# Revit family: R-MBS-225
name_source: partatom
category: Portes
units: mm (PartAtom-declared; Revit-internal decimal feet)

## family parameters
Couper avec des vides une fois chargée = Non
Hôte = Mur
Numéro OmniClass = 23.30.10.00
Partagée = Non
Repère de localisation dans la pièce = Non
Titre OmniClass = Doors
Toujours verticalement = Oui

## types (2) — shared parameters
Coloris parclose oculus = Acier, finition peinture thermolaque, gris, brillant
Construction analytique = <Aucun>
Définir les propriétés thermiques par = Type schématique
Epaisseur mur support = 146 mm
Epaisseur vantail = 40 mm  [stored 0.131234 ft]
Fermeture du mur = Par hôte
Fonction = Intérieur
Hauteur = 2000 mm  [stored 6.56168 ft]
Hauteur axe poignée = 1045 mm  [stored 3.42848 ft]
Hauteur bas support = 2020 mm  [stored 6.6273 ft]
Hauteur vantail souhaité = 2040 mm  [stored 6.69291 ft]
Largeur = 810 mm  [stored 2.65748 ft]
Largeur axe poignée = 50 mm  [stored 0.164042 ft]
Largeur du cadre = 75 mm  [stored 0.246063 ft]
Largeur hors tout = 810 mm  [stored 2.65748 ft]
Largeur vantail souhaitée = 830 mm  [stored 2.7231 ft]
Poignée = Oui
Projection - Ext. de l'encadrement = 25 mm  [stored 0.082021 ft]
Projection Int. de l'encadrement = 25 mm  [stored 0.082021 ft]

## per-type parameters (varying)
| type | Description | Fabricant | Finition chant | Modèle | Note d'identification | Porte encastrée | URL |
| 02 - Bois coulissante | Porte bois coulissante NUOVA âme pleine 1 vantail à rive droite | MALERBA | MDF noir | 1V NUOVA AP COUL | 1V NUOVA - AME PLEINE COULISSANTE | Non | https://www.malerba.fr |
| 02 - Bois coulissante à galandage |  |  | <Par catégorie> |  |  | Oui |  |

note: [stored X ft] marks values corroborated as IEEE doubles in the binary element streams (Revit-internal decimal feet)

## geometry (parser evidence)
native form markers: Blend x12
no freeform markers — native parametric forms only
